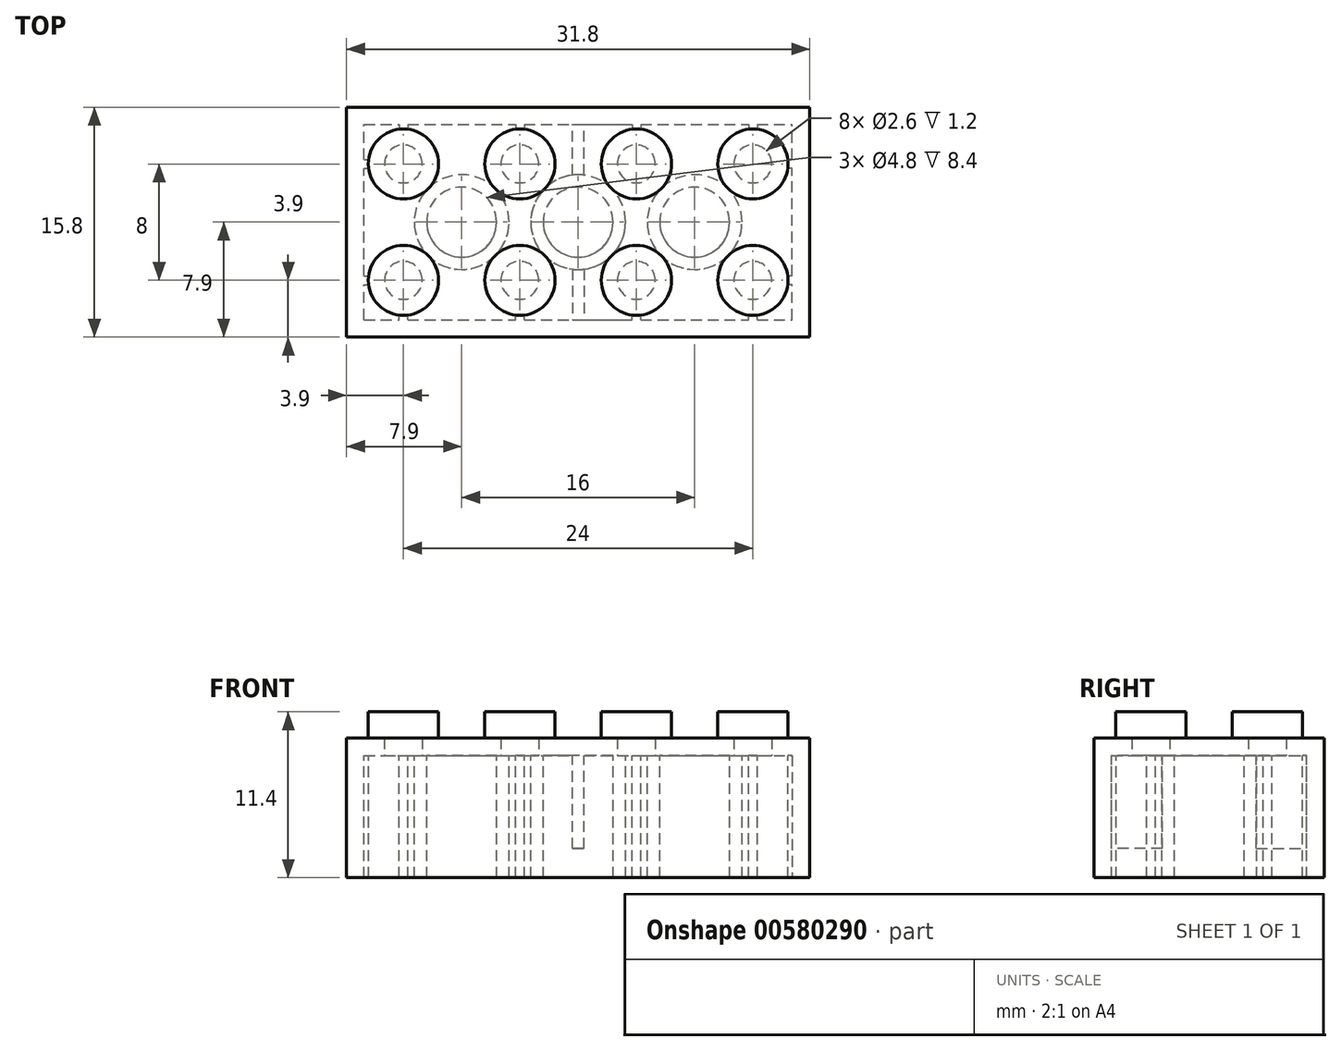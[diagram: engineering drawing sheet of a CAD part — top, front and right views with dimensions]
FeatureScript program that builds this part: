
annotation { "Feature Type Name" : "Feature", "Feature Type Description" : "" }
export const myFeature = defineFeature(function(context is Context, id is Id, definition is map)
    precondition{}
    {
        {
            var Q0;
            Q0=qCreatedBy(makeId("Top.planeOp"),FACE);
            var sketch = newSketch(context, id + "F0", { "sketchPlane" : qUnion([Q0])});
            skLineSegment(sketch, "E0.bottom", {"start": v(-15.9, 7.9) * mm, "end": v(15.9, 7.9) * mm});
            skLineSegment(sketch, "E0.top", {"start": v(-15.9, -7.9) * mm, "end": v(15.9, -7.9) * mm});
            skLineSegment(sketch, "E0.left", {"start": v(-15.9, 7.9) * mm, "end": v(-15.9, -7.9) * mm});
            skLineSegment(sketch, "E0.right", {"start": v(15.9, 7.9) * mm, "end": v(15.9, -7.9) * mm});
            skSolve(sketch);
        }
        {
            var Q0;
            Q0=makeQuery(id+"F0.imprint","IMPRINT",FACE,{"disambiguationData":[TD([[makeQuery(id+"F0.imprint","IMPRINT",EDGE,{"derivedFrom":sQuery(id+"F0.wireOp",EDGE,"E0.bottom")}),-1.0]])]});
            extrude(context, id + "F1", {"entities" : qUnion([Q0]), "endBound" : BoundingType.SYMMETRIC, "oppositeDirection" : true, "depth" : 9.6 * mm, "offsetDistance" : 25 * mm});
        }
        {
            var Q0;
            Q0=makeQuery(id+"F1.opExtrude","CAP_FACE",FACE,{"disambiguationData":[OSD([sQuery(id+"F0.wireOp",EDGE,"E0.bottom"),sQuery(id+"F0.wireOp",EDGE,"E0.top"),sQuery(id+"F0.wireOp",EDGE,"E0.left"),sQuery(id+"F0.wireOp",EDGE,"E0.right")])],"isStart":false});
            var sketch = newSketch(context, id + "F2", { "sketchPlane" : qUnion([Q0])});
            skLineSegment(sketch, "E1.bottom", {"start": v(-14.7, 6.7) * mm, "end": v(14.7, 6.7) * mm});
            skLineSegment(sketch, "E1.top", {"start": v(-14.7, -6.7) * mm, "end": v(14.7, -6.7) * mm});
            skLineSegment(sketch, "E1.left", {"start": v(-14.7, 6.7) * mm, "end": v(-14.7, -6.7) * mm});
            skLineSegment(sketch, "E1.right", {"start": v(14.7, 6.7) * mm, "end": v(14.7, -6.7) * mm});
            skPoint(sketch, "E1.middle", {"position": v(0, 0) * mm});
            skSolve(sketch);
        }
        {
            var Q0;
            Q0 = qSketchRegion(id + "F2", true);
            extrude(context, id + "F3", {"entities" : qUnion([Q0]), "operationType" : NewBodyOperationType.REMOVE, "oppositeDirection" : true, "depth" : 8.4 * mm, "offsetDistance" : 25 * mm});
        }
        {
            var Q0;
            Q0=makeQuery(id+"F1.opExtrude","CAP_FACE",FACE,{"disambiguationData":[OSD([sQuery(id+"F0.wireOp",EDGE,"E0.bottom"),sQuery(id+"F0.wireOp",EDGE,"E0.top"),sQuery(id+"F0.wireOp",EDGE,"E0.left"),sQuery(id+"F0.wireOp",EDGE,"E0.right")])],"isStart":true});
            var sketch = newSketch(context, id + "F4", { "sketchPlane" : qUnion([Q0])});
            skCircle(sketch, "E2", {"center": v(-12, 4) * mm, "radius": 2.4 * mm});
            skCircle(sketch, "E3", {"center": v(-4, 4) * mm, "radius": 2.4 * mm});
            skCircle(sketch, "E4.MirrorC", {"center": v(-4, -4) * mm, "radius": 2.4 * mm});
            skCircle(sketch, "E5.MirrorC", {"center": v(-12, -4) * mm, "radius": 2.4 * mm});
            skCircle(sketch, "E6.MirrorC", {"center": v(4, -4) * mm, "radius": 2.4 * mm});
            skCircle(sketch, "E7.MirrorC", {"center": v(12, -4) * mm, "radius": 2.4 * mm});
            skCircle(sketch, "E8.MirrorC", {"center": v(4, 4) * mm, "radius": 2.4 * mm});
            skCircle(sketch, "E9.MirrorC", {"center": v(12, 4) * mm, "radius": 2.4 * mm});
            skSolve(sketch);
        }
        {
            var Q0;
            Q0 = qSketchRegion(id + "F4", true);
            extrude(context, id + "F5", {"entities" : qUnion([Q0]), "operationType" : NewBodyOperationType.ADD, "depth" : 1.8 * mm, "offsetDistance" : 25 * mm});
        }
        {
            var Q0;
            Q0=makeQuery(id+"F3.boolean.opBoolean","COPY",FACE,{"derivedFrom":makeQuery(id+"F3.opExtrude","CAP_FACE",FACE,{"disambiguationData":[OSD([sQuery(id+"F2.wireOp",EDGE,"E1.bottom"),sQuery(id+"F2.wireOp",EDGE,"E1.top"),sQuery(id+"F2.wireOp",EDGE,"E1.left"),sQuery(id+"F2.wireOp",EDGE,"E1.right")])],"isStart":false})});
            var sketch = newSketch(context, id + "F6", { "sketchPlane" : qUnion([Q0])});
            skCircle(sketch, "E10", {"center": v(-12, 4) * mm, "radius": 1.3 * mm});
            skCircle(sketch, "E11", {"center": v(-4, 4) * mm, "radius": 1.3 * mm});
            skCircle(sketch, "E12.MirrorC", {"center": v(-4, -4) * mm, "radius": 1.3 * mm});
            skCircle(sketch, "E13.MirrorC", {"center": v(-12, -4) * mm, "radius": 1.3 * mm});
            skCircle(sketch, "E14.MirrorC", {"center": v(4, -4) * mm, "radius": 1.3 * mm});
            skCircle(sketch, "E15.MirrorC", {"center": v(12, -4) * mm, "radius": 1.3 * mm});
            skCircle(sketch, "E16.MirrorC", {"center": v(4, 4) * mm, "radius": 1.3 * mm});
            skCircle(sketch, "E17.MirrorC", {"center": v(12, 4) * mm, "radius": 1.3 * mm});
            skSolve(sketch);
        }
        {
            var Q0;
            Q0 = qSketchRegion(id + "F6", true);
            extrude(context, id + "F7", {"entities" : qUnion([Q0]), "operationType" : NewBodyOperationType.REMOVE, "oppositeDirection" : true, "depth" : 1.2 * mm, "offsetDistance" : 25 * mm});
        }
        {
            var Q0;
            Q0=makeQuery(id+"F3.boolean.opBoolean","COPY",FACE,{"derivedFrom":makeQuery(id+"F3.opExtrude","CAP_FACE",FACE,{"disambiguationData":[OSD([sQuery(id+"F2.wireOp",EDGE,"E1.bottom"),sQuery(id+"F2.wireOp",EDGE,"E1.top"),sQuery(id+"F2.wireOp",EDGE,"E1.left"),sQuery(id+"F2.wireOp",EDGE,"E1.right")])],"isStart":false})});
            var sketch = newSketch(context, id + "F8", { "sketchPlane" : qUnion([Q0])});
            skPoint(sketch, "E18", {"position": v(-12, 4) * mm});
            skPoint(sketch, "E19", {"position": v(-4, 4) * mm});
            skPoint(sketch, "E20", {"position": v(4, 4) * mm});
            skPoint(sketch, "E21", {"position": v(12, 4) * mm});
            skPoint(sketch, "E22", {"position": v(12, -4) * mm});
            skPoint(sketch, "E23", {"position": v(4, -4) * mm});
            skPoint(sketch, "E24", {"position": v(-4, -4) * mm});
            skPoint(sketch, "E25", {"position": v(-12, -4) * mm});
            skLineSegment(sketch, "E26", {"start": v(-12, 4) * mm, "end": v(-4, -4) * mm, "construction": true});
            skLineSegment(sketch, "E27", {"start": v(-4, 4) * mm, "end": v(-12, -4) * mm, "construction": true});
            skLineSegment(sketch, "E28", {"start": v(4, 4) * mm, "end": v(12, -4) * mm, "construction": true});
            skLineSegment(sketch, "E29", {"start": v(12, 4) * mm, "end": v(4, -4) * mm, "construction": true});
            skLineSegment(sketch, "E30", {"start": v(-4, 4) * mm, "end": v(4, -4) * mm, "construction": true});
            skLineSegment(sketch, "E31", {"start": v(4, 4) * mm, "end": v(-4, -4) * mm, "construction": true});
            skPoint(sketch, "E32", {"position": v(-8, 0) * mm});
            skPoint(sketch, "E33", {"position": v(8, 0) * mm});
            skPoint(sketch, "E34", {"position": v(0, 0) * mm});
            skCircle(sketch, "E35", {"center": v(-8, 0) * mm, "radius": 3.25 * mm});
            skCircle(sketch, "E36", {"center": v(0, 0) * mm, "radius": 3.25 * mm});
            skCircle(sketch, "E37", {"center": v(8, 0) * mm, "radius": 3.25 * mm});
            skCircle(sketch, "E38", {"center": v(-8, 0) * mm, "radius": 2.4 * mm});
            skCircle(sketch, "E39", {"center": v(0, 0) * mm, "radius": 2.4 * mm});
            skCircle(sketch, "E40", {"center": v(8, 0) * mm, "radius": 2.4 * mm});
            skSolve(sketch);
        }
        {
            var Q0;
            Q0 = qSketchRegion(id + "F8", true);
            var Q1;
            Q1=makeQuery(id+"F1.opExtrude","CAP_FACE",FACE,{"disambiguationData":[OSD([sQuery(id+"F0.wireOp",EDGE,"E0.bottom"),sQuery(id+"F0.wireOp",EDGE,"E0.top"),sQuery(id+"F0.wireOp",EDGE,"E0.left"),sQuery(id+"F0.wireOp",EDGE,"E0.right")])],"isStart":false});
            extrude(context, id + "F9", {"entities" : qUnion([Q0]), "operationType" : NewBodyOperationType.ADD, "endBound" : BoundingType.UP_TO_SURFACE, "depth" : 25 * mm, "endBoundEntityFace" : qUnion([Q1]), "offsetDistance" : 25 * mm});
        }
        {
            var Q0;
            Q0=makeQuery(id+"F3.boolean.opBoolean","COPY",FACE,{"derivedFrom":makeQuery(id+"F3.opExtrude","CAP_FACE",FACE,{"disambiguationData":[OSD([sQuery(id+"F2.wireOp",EDGE,"E1.bottom"),sQuery(id+"F2.wireOp",EDGE,"E1.top"),sQuery(id+"F2.wireOp",EDGE,"E1.left"),sQuery(id+"F2.wireOp",EDGE,"E1.right")])],"isStart":false})});
            var sketch = newSketch(context, id + "F10", { "sketchPlane" : qUnion([Q0])});
            skPoint(sketch, "E41", {"position": v(-8, 0) * mm});
            skPoint(sketch, "E42", {"position": v(8, 0) * mm});
            skPoint(sketch, "E43", {"position": v(-12, 4) * mm});
            skPoint(sketch, "E44", {"position": v(-4, 4) * mm});
            skPoint(sketch, "E45", {"position": v(4, 4) * mm});
            skPoint(sketch, "E46", {"position": v(12, 4) * mm});
            skPoint(sketch, "E47", {"position": v(12, -4) * mm});
            skPoint(sketch, "E48", {"position": v(4, -4) * mm});
            skPoint(sketch, "E49", {"position": v(-4, -4) * mm});
            skPoint(sketch, "E50", {"position": v(-12, -4) * mm});
            skLineSegment(sketch, "E51", {"start": v(-12, 4) * mm, "end": v(-29.94, 4) * mm, "construction": true});
            skLineSegment(sketch, "E52.bottom", {"start": v(-14.7, 3.7) * mm, "end": v(-14.4, 3.7) * mm});
            skLineSegment(sketch, "E52.top", {"start": v(-14.7, 4.3) * mm, "end": v(-14.4, 4.3) * mm});
            skLineSegment(sketch, "E52.left", {"start": v(-14.7, 3.7) * mm, "end": v(-14.7, 4.3) * mm});
            skLineSegment(sketch, "E52.right", {"start": v(-14.4, 3.7) * mm, "end": v(-14.4, 4.3) * mm});
            skLineSegment(sketch, "E53.MirrorCS", {"start": v(-14.7, -3.7) * mm, "end": v(-14.4, -3.7) * mm});
            skLineSegment(sketch, "E54.MirrorCS", {"start": v(-14.4, -3.7) * mm, "end": v(-14.4, -4.3) * mm});
            skLineSegment(sketch, "E55.MirrorCS", {"start": v(-14.7, -3.7) * mm, "end": v(-14.7, -4.3) * mm});
            skLineSegment(sketch, "E56.MirrorCS", {"start": v(-14.7, -4.3) * mm, "end": v(-14.4, -4.3) * mm});
            skLineSegment(sketch, "E57.MirrorCS", {"start": v(14.7, 3.7) * mm, "end": v(14.4, 3.7) * mm});
            skLineSegment(sketch, "E58.MirrorCS", {"start": v(14.4, 3.7) * mm, "end": v(14.4, 4.3) * mm});
            skLineSegment(sketch, "E59.MirrorCS", {"start": v(14.7, 4.3) * mm, "end": v(14.4, 4.3) * mm});
            skLineSegment(sketch, "E60.MirrorCS", {"start": v(14.7, 3.7) * mm, "end": v(14.7, 4.3) * mm});
            skLineSegment(sketch, "E61.MirrorCS", {"start": v(14.7, -4.3) * mm, "end": v(14.4, -4.3) * mm});
            skLineSegment(sketch, "E62.MirrorCS", {"start": v(14.4, -3.7) * mm, "end": v(14.4, -4.3) * mm});
            skLineSegment(sketch, "E63.MirrorCS", {"start": v(14.7, -3.7) * mm, "end": v(14.4, -3.7) * mm});
            skLineSegment(sketch, "E64.MirrorCS", {"start": v(14.7, -3.7) * mm, "end": v(14.7, -4.3) * mm});
            skSolve(sketch);
        }
        {
            var Q0;
            Q0 = qSketchRegion(id + "F10", true);
            var Q1;
            Q1=makeQuery(id+"F1.opExtrude","CAP_FACE",FACE,{"disambiguationData":[OSD([sQuery(id+"F0.wireOp",EDGE,"E0.bottom"),sQuery(id+"F0.wireOp",EDGE,"E0.top"),sQuery(id+"F0.wireOp",EDGE,"E0.left"),sQuery(id+"F0.wireOp",EDGE,"E0.right")])],"isStart":false});
            extrude(context, id + "F11", {"entities" : qUnion([Q0]), "operationType" : NewBodyOperationType.ADD, "endBound" : BoundingType.UP_TO_SURFACE, "depth" : 25 * mm, "endBoundEntityFace" : qUnion([Q1]), "offsetDistance" : 25 * mm});
        }
        {
            var Q0;
            {var subQ0=sQuery(id+"F2.wireOp",EDGE,"E1.left");var subQ1=sQuery(id+"F2.wireOp",EDGE,"E1.bottom");var subQ2=sQuery(id+"F2.wireOp",EDGE,"E1.top");var subQ3=sQuery(id+"F2.wireOp",EDGE,"E1.right");Q0=makeQuery(id+"F9.boolean.opBoolean","SPLIT",FACE,{"disambiguationData":[TD([makeQuery(id+"F3.boolean.opBoolean","COPY",FACE,{"derivedFrom":makeQuery(id+"F3.opExtrude","SWEPT_FACE",FACE,{"disambiguationData":[OSD([subQ1])]})})])],"derivedFrom":makeQuery(id+"F3.boolean.opBoolean","COPY",FACE,{"derivedFrom":makeQuery(id+"F3.opExtrude","CAP_FACE",FACE,{"disambiguationData":[OSD([subQ1,subQ2,subQ0,subQ3])],"isStart":false})})});}
            var sketch = newSketch(context, id + "F12", { "sketchPlane" : qUnion([Q0])});
            skPoint(sketch, "E65", {"position": v(-12, 4) * mm});
            skLineSegment(sketch, "E66", {"start": v(-12, 4) * mm, "end": v(-12, 11.05) * mm, "construction": true});
            skLineSegment(sketch, "E67.bottom", {"start": v(-12.3, 6.7) * mm, "end": v(-11.7, 6.7) * mm});
            skLineSegment(sketch, "E67.top", {"start": v(-12.3, 6.4) * mm, "end": v(-11.7, 6.4) * mm});
            skLineSegment(sketch, "E67.left", {"start": v(-12.3, 6.7) * mm, "end": v(-12.3, 6.4) * mm});
            skLineSegment(sketch, "E67.right", {"start": v(-11.7, 6.7) * mm, "end": v(-11.7, 6.4) * mm});
            skLineSegment(sketch, "E68.MirrorCS", {"start": v(-11.7, -6.7) * mm, "end": v(-11.7, -6.4) * mm});
            skLineSegment(sketch, "E69.MirrorCS", {"start": v(-12.3, -6.7) * mm, "end": v(-11.7, -6.7) * mm});
            skLineSegment(sketch, "E70.MirrorCS", {"start": v(-12.3, -6.7) * mm, "end": v(-12.3, -6.4) * mm});
            skLineSegment(sketch, "E71.MirrorCS", {"start": v(-12.3, -6.4) * mm, "end": v(-11.7, -6.4) * mm});
            skPoint(sketch, "E72", {"position": v(-8, 0) * mm});
            skLineSegment(sketch, "E73", {"start": v(-8, 0) * mm, "end": v(-8, 10.81) * mm, "construction": true});
            skLineSegment(sketch, "E74.MirrorCS", {"start": v(-3.7, 6.7) * mm, "end": v(-3.7, 6.4) * mm});
            skLineSegment(sketch, "E75.MirrorCS", {"start": v(-3.7, 6.4) * mm, "end": v(-4.3, 6.4) * mm});
            skLineSegment(sketch, "E76.MirrorCS", {"start": v(-4.3, 6.7) * mm, "end": v(-4.3, 6.4) * mm});
            skLineSegment(sketch, "E77.MirrorCS", {"start": v(-3.7, 6.7) * mm, "end": v(-4.3, 6.7) * mm});
            skLineSegment(sketch, "E78.MirrorCS", {"start": v(-3.7, -6.7) * mm, "end": v(-3.7, -6.4) * mm});
            skLineSegment(sketch, "E79.MirrorCS", {"start": v(-3.7, -6.7) * mm, "end": v(-4.3, -6.7) * mm});
            skLineSegment(sketch, "E80.MirrorCS", {"start": v(-4.3, -6.7) * mm, "end": v(-4.3, -6.4) * mm});
            skLineSegment(sketch, "E81.MirrorCS", {"start": v(-3.7, -6.4) * mm, "end": v(-4.3, -6.4) * mm});
            skLineSegment(sketch, "E82.MirrorCS", {"start": v(4.3, 6.7) * mm, "end": v(4.3, 6.4) * mm});
            skLineSegment(sketch, "E83.MirrorCS", {"start": v(3.7, 6.7) * mm, "end": v(4.3, 6.7) * mm});
            skLineSegment(sketch, "E84.MirrorCS", {"start": v(3.7, 6.7) * mm, "end": v(3.7, 6.4) * mm});
            skLineSegment(sketch, "E85.MirrorCS", {"start": v(3.7, 6.4) * mm, "end": v(4.3, 6.4) * mm});
            skLineSegment(sketch, "E86.MirrorCS", {"start": v(12.3, 6.7) * mm, "end": v(12.3, 6.4) * mm});
            skLineSegment(sketch, "E87.MirrorCS", {"start": v(12.3, 6.4) * mm, "end": v(11.7, 6.4) * mm});
            skLineSegment(sketch, "E88.MirrorCS", {"start": v(11.7, 6.7) * mm, "end": v(11.7, 6.4) * mm});
            skLineSegment(sketch, "E89.MirrorCS", {"start": v(12.3, 6.7) * mm, "end": v(11.7, 6.7) * mm});
            skLineSegment(sketch, "E90.MirrorCS", {"start": v(12.3, -6.7) * mm, "end": v(11.7, -6.7) * mm});
            skLineSegment(sketch, "E91.MirrorCS", {"start": v(11.7, -6.7) * mm, "end": v(11.7, -6.4) * mm});
            skLineSegment(sketch, "E92.MirrorCS", {"start": v(12.3, -6.4) * mm, "end": v(11.7, -6.4) * mm});
            skLineSegment(sketch, "E93.MirrorCS", {"start": v(12.3, -6.7) * mm, "end": v(12.3, -6.4) * mm});
            skLineSegment(sketch, "E94.MirrorCS", {"start": v(3.7, -6.7) * mm, "end": v(4.3, -6.7) * mm});
            skLineSegment(sketch, "E95.MirrorCS", {"start": v(3.7, -6.7) * mm, "end": v(3.7, -6.4) * mm});
            skLineSegment(sketch, "E96.MirrorCS", {"start": v(3.7, -6.4) * mm, "end": v(4.3, -6.4) * mm});
            skLineSegment(sketch, "E97.MirrorCS", {"start": v(4.3, -6.7) * mm, "end": v(4.3, -6.4) * mm});
            skSolve(sketch);
        }
        {
            var Q0;
            Q0 = qSketchRegion(id + "F12", true);
            var Q1;
            {var subQ0=sQuery(id+"F0.wireOp",EDGE,"E0.right");var subQ1=sQuery(id+"F0.wireOp",EDGE,"E0.left");var subQ2=sQuery(id+"F0.wireOp",EDGE,"E0.top");var subQ3=sQuery(id+"F0.wireOp",EDGE,"E0.bottom");Q1=makeQuery(id+"F11.boolean.opBoolean","MERGE",FACE,{"derivedFrom":[makeQuery(id+"F1.opExtrude","CAP_FACE",FACE,{"disambiguationData":[OSD([subQ3,subQ2,subQ1,subQ0])],"isStart":false}),makeQuery(id+"F11.opExtrude","CAP_FACE",FACE,{"disambiguationData":[OSD([subQ3,subQ2,subQ1,subQ0]),OD(0.0)],"isStart":false}),makeQuery(id+"F11.opExtrude","CAP_FACE",FACE,{"disambiguationData":[OSD([subQ3,subQ2,subQ1,subQ0]),OD(1.0)],"isStart":false}),makeQuery(id+"F11.opExtrude","CAP_FACE",FACE,{"disambiguationData":[OSD([subQ3,subQ2,subQ1,subQ0]),OD(2.0)],"isStart":false}),makeQuery(id+"F11.opExtrude","CAP_FACE",FACE,{"disambiguationData":[OSD([subQ3,subQ2,subQ1,subQ0]),OD(3.0)],"isStart":false})]});}
            extrude(context, id + "F13", {"entities" : qUnion([Q0]), "operationType" : NewBodyOperationType.ADD, "endBound" : BoundingType.UP_TO_SURFACE, "depth" : 25 * mm, "endBoundEntityFace" : qUnion([Q1]), "offsetDistance" : 25 * mm});
        }
        {
            var Q0;
            {var subQ0=sQuery(id+"F2.wireOp",EDGE,"E1.left");var subQ1=sQuery(id+"F2.wireOp",EDGE,"E1.bottom");var subQ2=sQuery(id+"F2.wireOp",EDGE,"E1.top");var subQ3=sQuery(id+"F2.wireOp",EDGE,"E1.right");Q0=makeQuery(id+"F9.boolean.opBoolean","SPLIT",FACE,{"disambiguationData":[TD([makeQuery(id+"F3.boolean.opBoolean","COPY",FACE,{"derivedFrom":makeQuery(id+"F3.opExtrude","SWEPT_FACE",FACE,{"disambiguationData":[OSD([subQ1])]})})])],"derivedFrom":makeQuery(id+"F3.boolean.opBoolean","COPY",FACE,{"derivedFrom":makeQuery(id+"F3.opExtrude","CAP_FACE",FACE,{"disambiguationData":[OSD([subQ1,subQ2,subQ0,subQ3])],"isStart":false})})});}
            var sketch = newSketch(context, id + "F14", { "sketchPlane" : qUnion([Q0])});
            skLineSegment(sketch, "E98", {"start": v(-0.4, 3.23) * mm, "end": v(-0.4, 6.7) * mm});
            skLineSegment(sketch, "E99", {"start": v(0.4, 3.23) * mm, "end": v(0.4, 6.7) * mm});
            skLineSegment(sketch, "E100.MirrorCS", {"start": v(0.4, -3.23) * mm, "end": v(0.4, -6.7) * mm});
            skLineSegment(sketch, "E101.MirrorCS", {"start": v(-0.4, -3.23) * mm, "end": v(-0.4, -6.7) * mm});
            skLineSegment(sketch, "E102", {"start": v(-0.4, 6.7) * mm, "end": v(0.4, 6.7) * mm});
            skLineSegment(sketch, "E103", {"start": v(-0.4, -3.23) * mm, "end": v(0.4, -3.23) * mm});
            skLineSegment(sketch, "E104", {"start": v(-0.4, 3.23) * mm, "end": v(0.4, 3.23) * mm});
            skLineSegment(sketch, "E105", {"start": v(-0.4, -6.7) * mm, "end": v(0.4, -6.7) * mm});
            skSolve(sketch);
        }
        {
            var Q0;
            Q0 = qSketchRegion(id + "F14", true);
            extrude(context, id + "F15", {"entities" : qUnion([Q0]), "operationType" : NewBodyOperationType.ADD, "depth" : 6.4 * mm, "offsetDistance" : 25 * mm});
        }
    });
